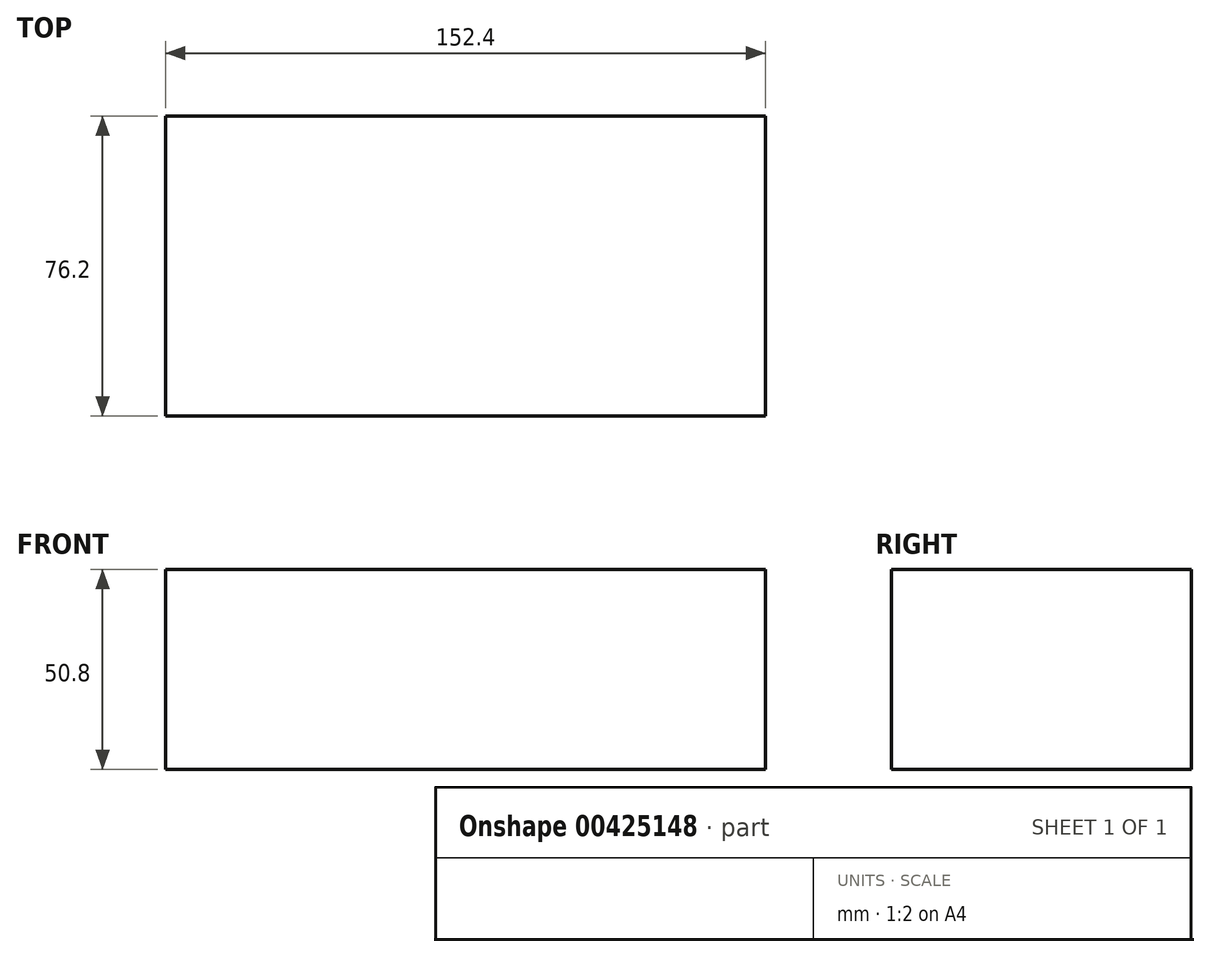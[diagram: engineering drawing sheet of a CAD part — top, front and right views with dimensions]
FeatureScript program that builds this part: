
annotation { "Feature Type Name" : "Feature", "Feature Type Description" : "" }
export const myFeature = defineFeature(function(context is Context, id is Id, definition is map)
    precondition{}
    {
        {
            var Q0;
            Q0=qCreatedBy(makeId("Top.planeOp"),FACE);
            var sketch = newSketch(context, id + "F0", { "sketchPlane" : qUnion([Q0])});
            skLineSegment(sketch, "E0", {"start": v(0, 0) * mm, "end": v(152.4, 0) * mm});
            skLineSegment(sketch, "E1", {"start": v(152.4, 0) * mm, "end": v(152.4, 76.2) * mm});
            skLineSegment(sketch, "E2", {"start": v(152.4, 76.2) * mm, "end": v(0, 76.2) * mm});
            skLineSegment(sketch, "E3", {"start": v(0, 76.2) * mm, "end": v(0, 0) * mm});
            skSolve(sketch);
        }
        {
            var Q0;
            Q0=makeQuery(id+"F0.imprint","IMPRINT",FACE,{"disambiguationData":[TD([[makeQuery(id+"F0.imprint","IMPRINT",EDGE,{"derivedFrom":sQuery(id+"F0.wireOp",EDGE,"E0")}),1.0]])]});
            extrude(context, id + "F1", {"entities" : qUnion([Q0]), "depth" : 50.8 * mm});
        }
        {
            var Q0;
            Q0=makeQuery(id+"F1.opExtrude","SWEPT_FACE",FACE,{"disambiguationData":[OSD([sQuery(id+"F0.wireOp",EDGE,"E0")])]});
            var sketch = newSketch(context, id + "F2", { "sketchPlane" : qUnion([Q0])});
            skLineSegment(sketch, "E4", {"start": v(152.4, 25.4) * mm, "end": v(101.6, 25.4) * mm});
            skLineSegment(sketch, "E5", {"start": v(101.6, 25.4) * mm, "end": v(101.6, 50.8) * mm});
            skLineSegment(sketch, "E6", {"start": v(101.6, 50.8) * mm, "end": v(152.4, 50.8) * mm});
            skLineSegment(sketch, "E7", {"start": v(152.4, 50.8) * mm, "end": v(152.4, 25.4) * mm});
            skSolve(sketch);
        }
        {
            var Q0;
            Q0 = qSketchRegion(id + "F2", true);
            extrude(context, id + "F3", {"entities" : qUnion([Q0]), "operationType" : NewBodyOperationType.ADD, "oppositeDirection" : true, "depth" : 33.53 * mm});
        }
    });
